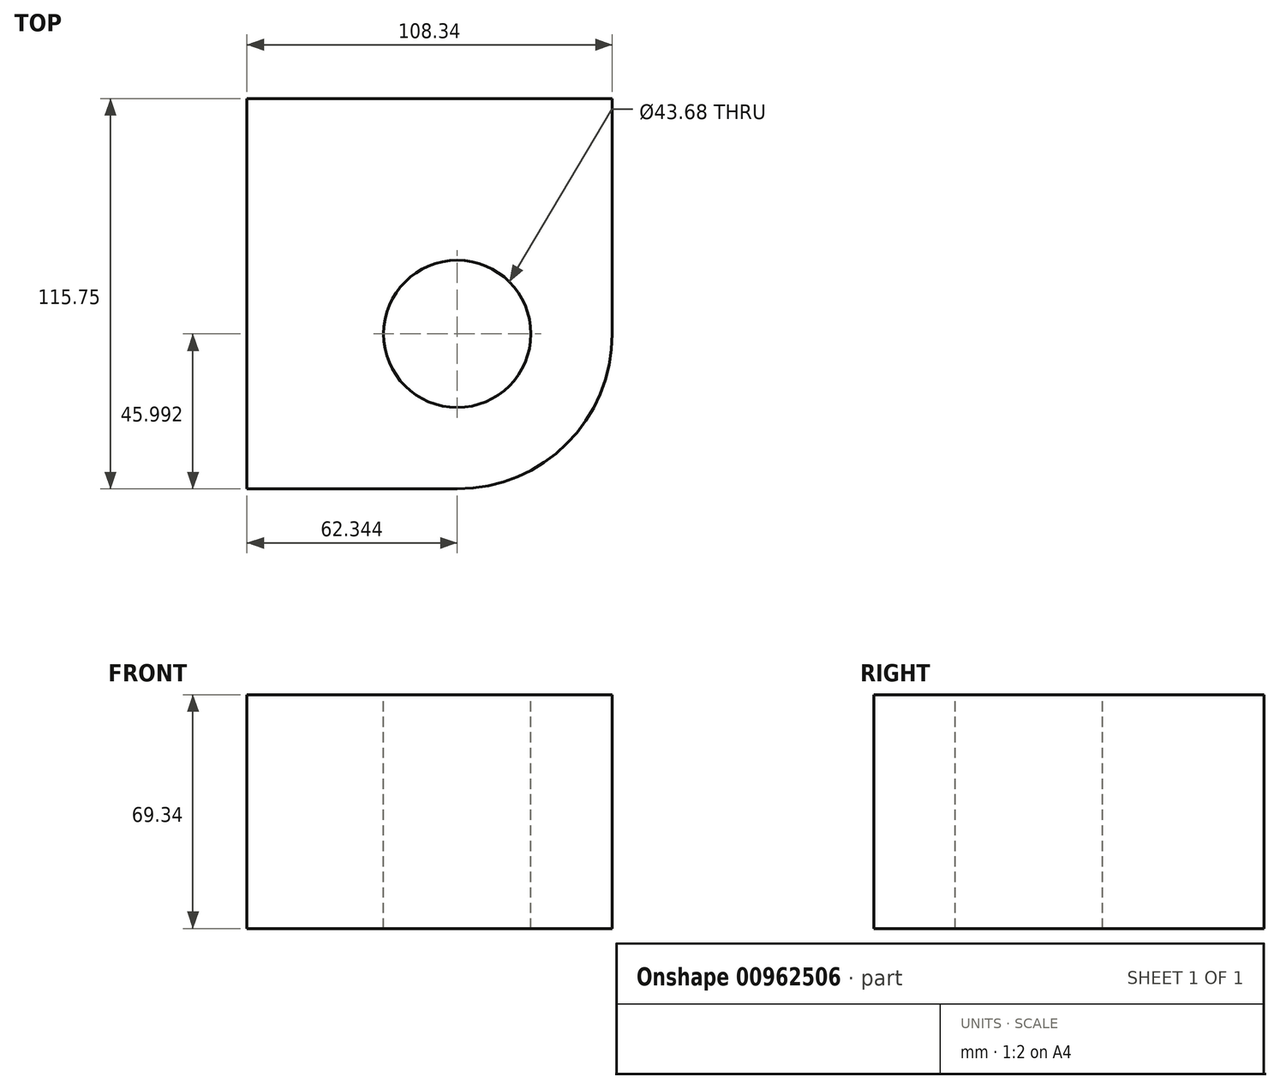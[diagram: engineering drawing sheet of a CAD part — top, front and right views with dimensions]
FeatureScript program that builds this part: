
annotation { "Feature Type Name" : "Feature", "Feature Type Description" : "" }
export const myFeature = defineFeature(function(context is Context, id is Id, definition is map)
    precondition{}
    {
        {
            var Q0;
            Q0=qCreatedBy(makeId("Top.planeOp"),FACE);
            var sketch = newSketch(context, id + "F0", { "sketchPlane" : qUnion([Q0])});
            skLineSegment(sketch, "E0.bottom", {"start": v(0, 0) * mm, "end": v(108.34, 0) * mm});
            skLineSegment(sketch, "E0.top", {"start": v(0, -115.75) * mm, "end": v(108.34, -115.75) * mm});
            skLineSegment(sketch, "E0.left", {"start": v(0, 0) * mm, "end": v(0, -115.75) * mm});
            skLineSegment(sketch, "E0.right", {"start": v(108.34, 0) * mm, "end": v(108.34, -115.75) * mm});
            skSolve(sketch);
        }
        {
            var Q0;
            Q0=makeQuery(id+"F0.imprint","IMPRINT",FACE,{"disambiguationData":[TD([[makeQuery(id+"F0.imprint","IMPRINT",EDGE,{"derivedFrom":sQuery(id+"F0.wireOp",EDGE,"E0.bottom")}),-1.0]])]});
            extrude(context, id + "F1", {"entities" : qUnion([Q0]), "depth" : 69.34 * mm, "offsetDistance" : 25.4 * mm});
        }
        {
            var Q0;
            Q0=makeQuery(id+"F1.opExtrude","SWEPT_EDGE",EDGE,{"disambiguationData":[OSD([sQuery(id+"F0.wireOp",EDGE,"E0.top"),sQuery(id+"F0.wireOp",EDGE,"E0.right")])]});
            fillet(context, id + "F2", {"entities" : qUnion([Q0]), "radius" : 46 * mm, "tangentPropagation" : true, "allowEdgeOverflow" : false});
        }
        {
            var Q0;
            Q0=makeQuery(id+"F1.opExtrude","CAP_FACE",FACE,{"disambiguationData":[OSD([sQuery(id+"F0.wireOp",EDGE,"E0.bottom"),sQuery(id+"F0.wireOp",EDGE,"E0.top"),sQuery(id+"F0.wireOp",EDGE,"E0.left"),sQuery(id+"F0.wireOp",EDGE,"E0.right")])],"isStart":false});
            var sketch = newSketch(context, id + "F3", { "sketchPlane" : qUnion([Q0])});
            skCircle(sketch, "E1", {"center": v(62.34, -69.76) * mm, "radius": 21.84 * mm});
            skSolve(sketch);
        }
        {
            var Q0;
            Q0=makeQuery(id+"F3.imprint","IMPRINT",FACE,{"disambiguationData":[TD([[makeQuery(id+"F3.imprint","IMPRINT",EDGE,{"derivedFrom":sQuery(id+"F3.wireOp",EDGE,"E1")}),1.0]])]});
            extrude(context, id + "F4", {"entities" : qUnion([Q0]), "operationType" : NewBodyOperationType.REMOVE, "oppositeDirection" : true, "depth" : 89.92 * mm, "offsetDistance" : 25.4 * mm});
        }
    });
